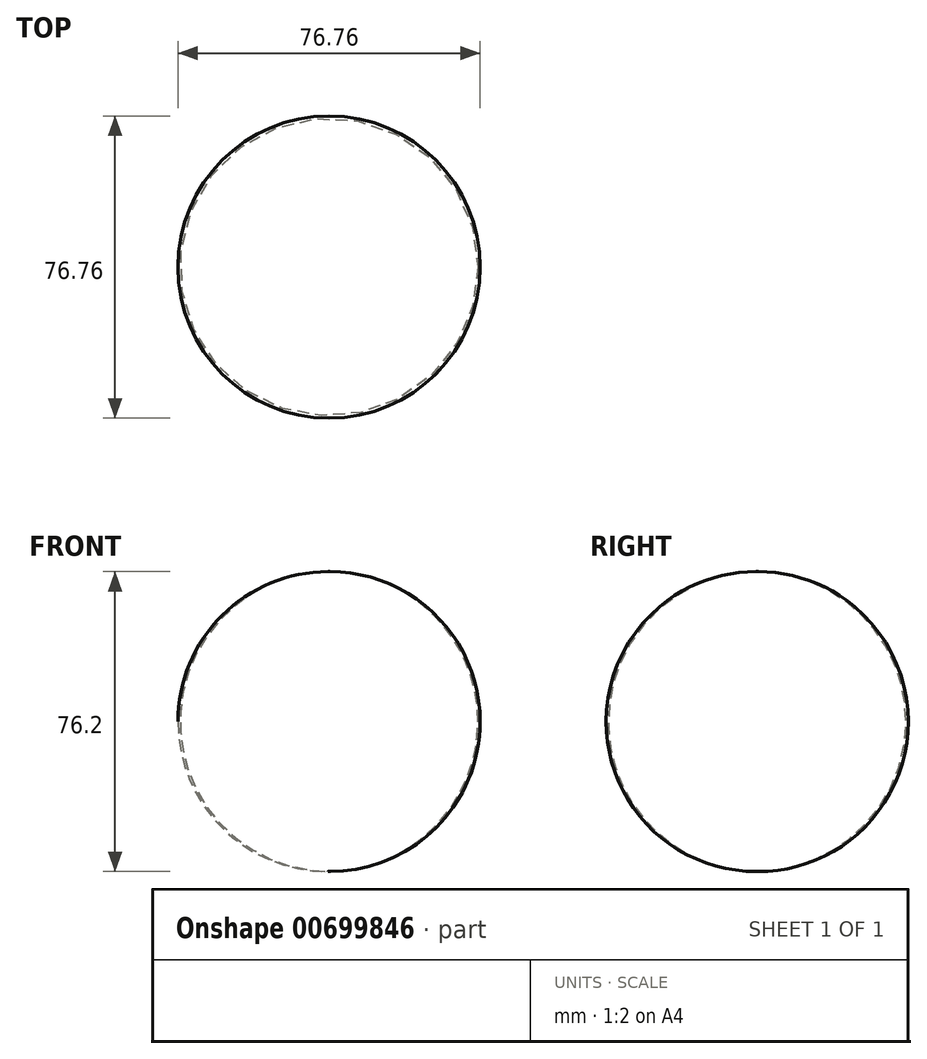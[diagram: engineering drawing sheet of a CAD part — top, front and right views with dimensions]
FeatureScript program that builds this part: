
annotation { "Feature Type Name" : "Feature", "Feature Type Description" : "" }
export const myFeature = defineFeature(function(context is Context, id is Id, definition is map)
    precondition{}
    {
        {
            var Q0;
            Q0=qCreatedBy(makeId("Right.planeOp"),FACE);
            var sketch = newSketch(context, id + "F0", { "sketchPlane" : qUnion([Q0])});
            skLineSegment(sketch, "E0", {"start": v(0, 0) * mm, "end": v(0, 76.2) * mm});
            skArc(sketch, "E1", {"start": v(0, 0) * mm, "mid": v(37.83, 38.1) * mm, "end": v(0, 76.2) * mm});
            skSolve(sketch);
        }
        {
            var Q0;
            Q0=makeQuery(id+"F0.imprint","IMPRINT",FACE,{"disambiguationData":[TD([[makeQuery(id+"F0.imprint","IMPRINT",EDGE,{"derivedFrom":sQuery(id+"F0.wireOp",EDGE,"E0")}),-1.0]])]});
            var Q1;
            Q1=sQuery(id+"F0.wireOp",EDGE,"E0");
            revolve(context, id + "F1", {"entities" : qUnion([Q0]), "axis" : qUnion([Q1]), "revolveType" : RevolveType.FULL});
        }
    });
